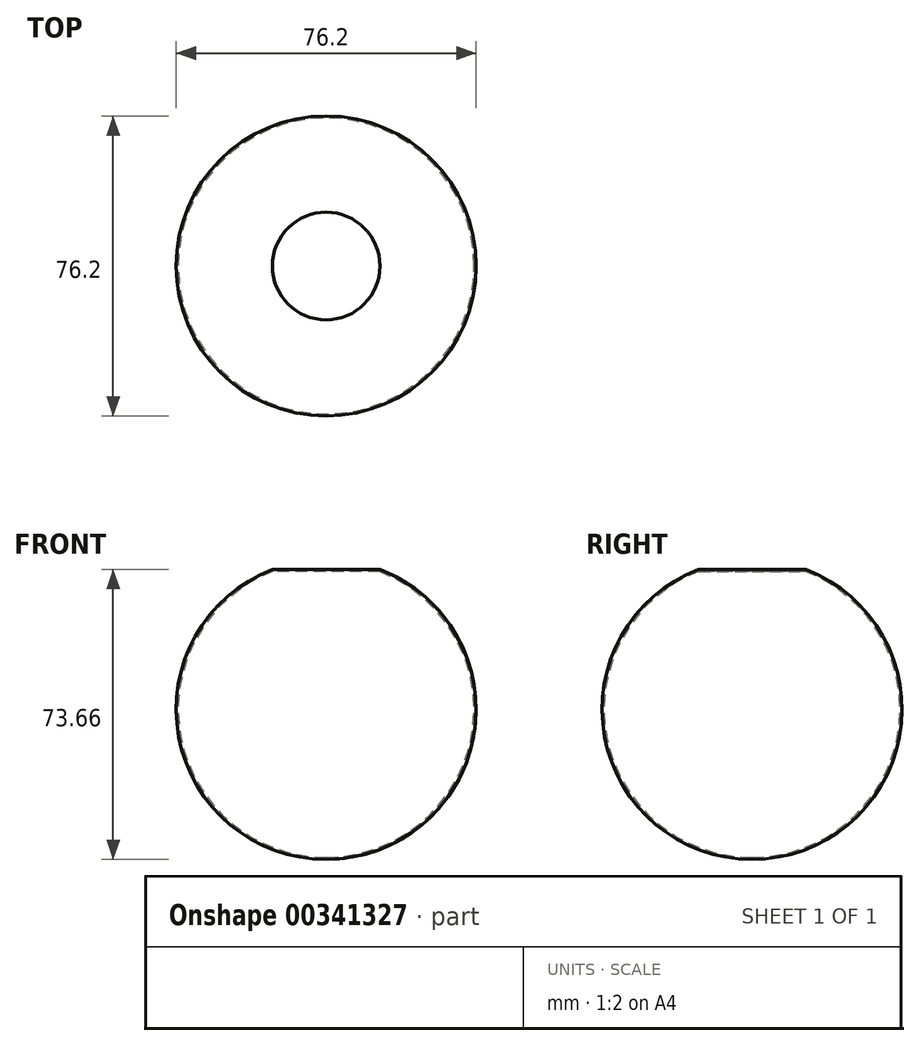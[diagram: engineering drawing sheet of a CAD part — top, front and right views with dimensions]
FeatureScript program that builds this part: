
annotation { "Feature Type Name" : "Feature", "Feature Type Description" : "" }
export const myFeature = defineFeature(function(context is Context, id is Id, definition is map)
    precondition{}
    {
        {
            var Q0;
            Q0=qCreatedBy(makeId("Front.planeOp"),FACE);
            var sketch = newSketch(context, id + "F0", { "sketchPlane" : qUnion([Q0])});
            skArc(sketch, "E0", {"start": v(0, -38.1) * mm, "mid": v(38.1, 0) * mm, "end": v(0, 38.1) * mm});
            skLineSegment(sketch, "E1", {"start": v(0, 38.1) * mm, "end": v(0, -38.1) * mm});
            skPoint(sketch, "E2.orphan", {"position": v(0, 50.14) * mm});
            skSolve(sketch);
        }
        {
            var Q0;
            Q0=makeQuery(id+"F0.imprint","IMPRINT",FACE,{"disambiguationData":[TD([[makeQuery(id+"F0.imprint","IMPRINT",EDGE,{"derivedFrom":sQuery(id+"F0.wireOp",EDGE,"E0")}),1.0]])]});
            var Q1;
            Q1=sQuery(id+"F0.wireOp",EDGE,"E1");
            revolve(context, id + "F1", {"entities" : qUnion([Q0]), "axis" : qUnion([Q1]), "revolveType" : RevolveType.FULL});
        }
        {
            var Q0;
            Q0=qCreatedBy(makeId("Top.planeOp"),FACE);
            cPlane(context, id + "F2", {"entities" : qUnion([Q0]), "cplaneType" : CPlaneType.OFFSET, "offset" : 35.56 * mm, "width" : 152.4 * mm, "height" : 152.4 * mm});
        }
        {
            var Q0;
            Q0=qCreatedBy(id+"F2.planeOp",FACE);
            var sketch = newSketch(context, id + "F3", { "sketchPlane" : qUnion([Q0])});
            skLineSegment(sketch, "E3.bottom", {"start": v(16.51, 16.51) * mm, "end": v(-16.51, 16.51) * mm});
            skLineSegment(sketch, "E3.top", {"start": v(16.51, -16.51) * mm, "end": v(-16.51, -16.51) * mm});
            skLineSegment(sketch, "E3.left", {"start": v(16.51, 16.51) * mm, "end": v(16.51, -16.51) * mm});
            skLineSegment(sketch, "E3.right", {"start": v(-16.51, 16.51) * mm, "end": v(-16.51, -16.51) * mm});
            skPoint(sketch, "E3.middle", {"position": v(0, 0) * mm});
            skSolve(sketch);
        }
        {
            var Q0;
            Q0=makeQuery(id+"F3.imprint","IMPRINT",FACE,{"disambiguationData":[TD([[makeQuery(id+"F3.imprint","IMPRINT",EDGE,{"derivedFrom":sQuery(id+"F3.wireOp",EDGE,"E3.bottom")}),1.0]])]});
            extrude(context, id + "F4", {"entities" : qUnion([Q0]), "operationType" : NewBodyOperationType.REMOVE, "depth" : 25.4 * mm});
        }
        {
            var Q0;
            Q0=makeQuery(id+"F4.boolean.opBoolean","COPY",FACE,{"derivedFrom":makeQuery(id+"F4.opExtrude","CAP_FACE",FACE,{"disambiguationData":[OSD([sQuery(id+"F3.wireOp",EDGE,"E3.bottom"),sQuery(id+"F3.wireOp",EDGE,"E3.top"),sQuery(id+"F3.wireOp",EDGE,"E3.left"),sQuery(id+"F3.wireOp",EDGE,"E3.right")])],"isStart":true})});
            var Q1;
            Q1=makeQuery(id+"F1.opRevolve","SWEPT_BODY",BODY,{"disambiguationData":[OSD([sQuery(id+"F0.wireOp",EDGE,"E0"),sQuery(id+"F0.wireOp",EDGE,"E1")])]});
            shell(context, id + "F5", {"isHollow" : true, "entities" : qUnion([Q0]), "parts" : qUnion([Q1]), "thickness" : .5 * mm});
        }
    });
